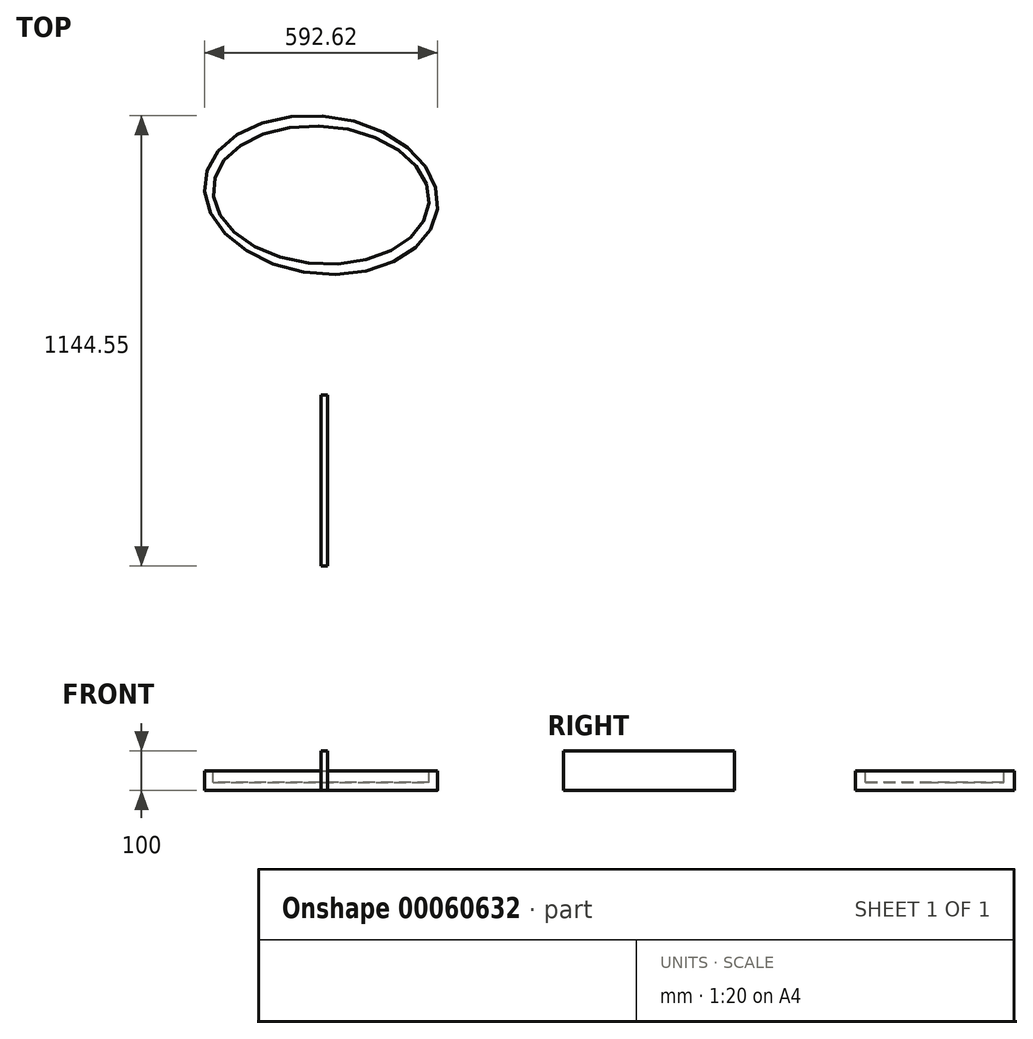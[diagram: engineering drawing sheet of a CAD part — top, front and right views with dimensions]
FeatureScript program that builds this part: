
annotation { "Feature Type Name" : "Feature", "Feature Type Description" : "" }
export const myFeature = defineFeature(function(context is Context, id is Id, definition is map)
    precondition{}
    {
        {
            var Q0;
            Q0=qCreatedBy(makeId("Right.planeOp"),FACE);
            var sketch = newSketch(context, id + "F0", { "sketchPlane" : qUnion([Q0])});
            skLineSegment(sketch, "E0.bottom", {"start": v(-434, 100) * mm, "end": v(0, 100) * mm});
            skLineSegment(sketch, "E0.top", {"start": v(-434, 0) * mm, "end": v(0, 0) * mm});
            skLineSegment(sketch, "E0.left", {"start": v(-434, 100) * mm, "end": v(-434, 0) * mm});
            skLineSegment(sketch, "E0.right", {"start": v(0, 100) * mm, "end": v(0, 0) * mm});
            skSolve(sketch);
        }
        {
            var Q0;
            Q0 = qSketchRegion(id + "F0", true);
            extrude(context, id + "F1", {"entities" : qUnion([Q0]), "depth" : 16 * mm});
        }
        {
            var Q0;
            Q0=qCreatedBy(makeId("Top.planeOp"),FACE);
            var sketch = newSketch(context, id + "F2", { "sketchPlane" : qUnion([Q0])});
            skEllipse(sketch, "E1", {"center": v(0, 508.8) * mm, "majorRadius": 297.5 * mm, "minorRadius": 200 * mm, "majorAxis": v(1, -0.12)});
            skSolve(sketch);
        }
        {
            var Q0;
            Q0=makeQuery(id+"F2.imprint","IMPRINT",FACE,{"disambiguationData":[TD([[makeQuery(id+"F2.imprint","IMPRINT",EDGE,{"derivedFrom":sQuery(id+"F2.wireOp",EDGE,"E1")}),1.0]])]});
            extrude(context, id + "F3", {"entities" : qUnion([Q0]), "depth" : 50 * mm});
        }
        {
            var Q0;
            Q0=makeQuery(id+"F3.opExtrude","CAP_FACE",FACE,{"disambiguationData":[OSD([sQuery(id+"F2.wireOp",EDGE,"E1")])],"isStart":false});
            var sketch = newSketch(context, id + "F4", { "sketchPlane" : qUnion([Q0])});
            skEllipse(sketch, "E2", {"center": v(0, 508.8) * mm, "majorRadius": 275 * mm, "minorRadius": 175 * mm, "majorAxis": v(1, -0.07)});
            skSolve(sketch);
        }
        {
            var Q0;
            Q0 = qSketchRegion(id + "F4", true);
            extrude(context, id + "F5", {"entities" : qUnion([Q0]), "operationType" : NewBodyOperationType.REMOVE, "oppositeDirection" : true, "depth" : 30 * mm});
        }
    });
